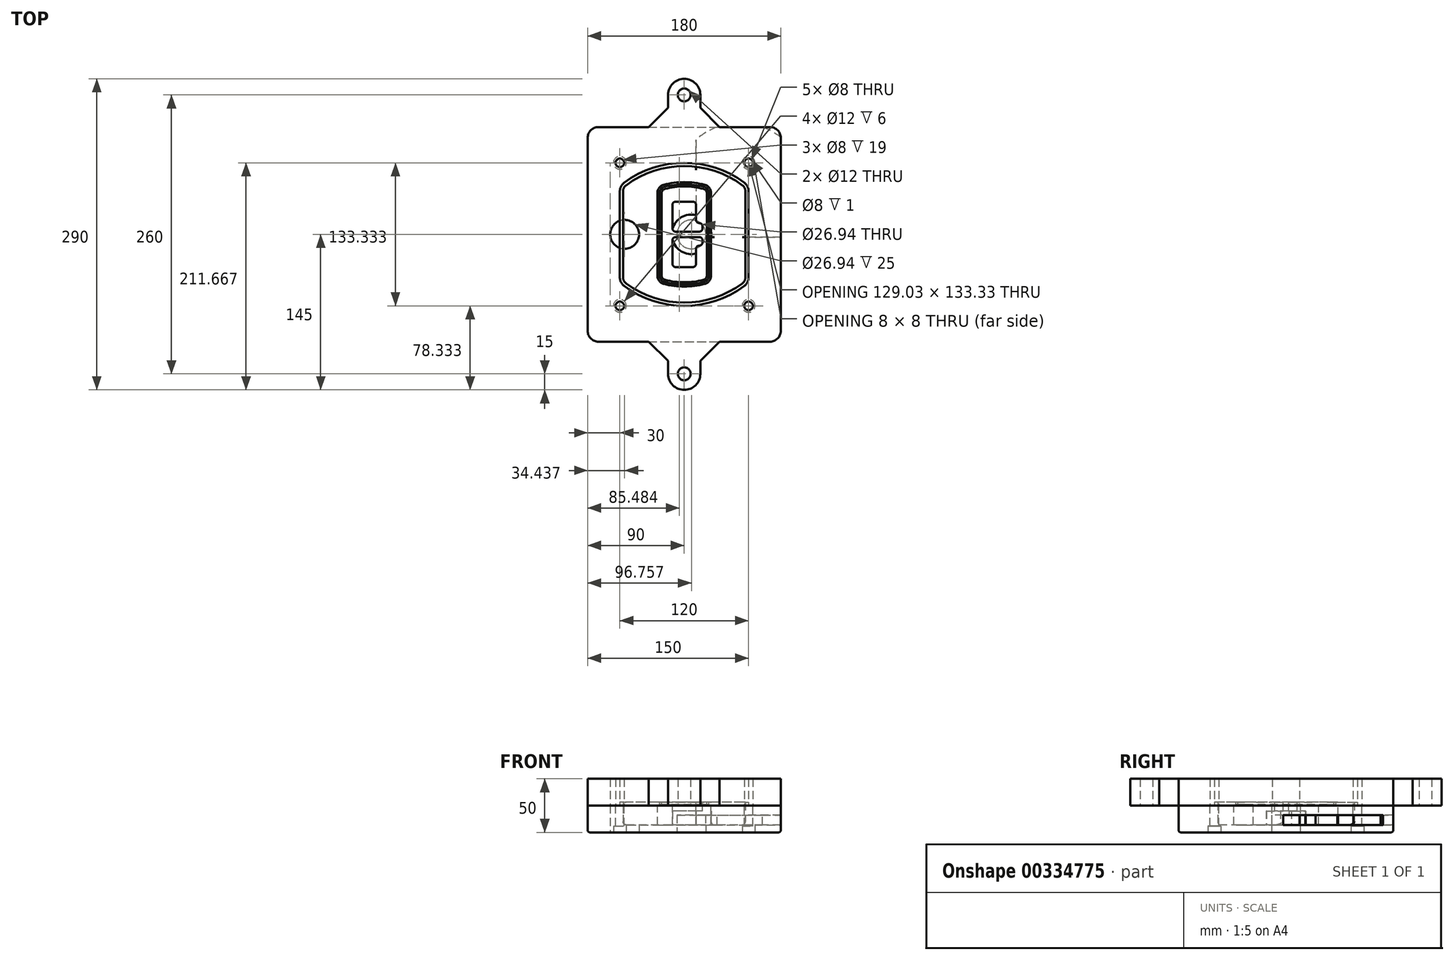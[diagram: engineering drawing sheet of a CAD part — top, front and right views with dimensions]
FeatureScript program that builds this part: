
annotation { "Feature Type Name" : "Feature", "Feature Type Description" : "" }
export const myFeature = defineFeature(function(context is Context, id is Id, definition is map)
    precondition{}
    {
        {
            var Q0;
            Q0=qCreatedBy(makeId("Top.planeOp"),FACE);
            var sketch = newSketch(context, id + "F0", { "sketchPlane" : qUnion([Q0])});
            skPoint(sketch, "E0.rect.middle", {"position": v(0, 0) * mm});
            skLineSegment(sketch, "E1.bottom", {"start": v(-80, -100) * mm, "end": v(80, -100) * mm});
            skLineSegment(sketch, "E1.top", {"start": v(-80, 100) * mm, "end": v(80, 100) * mm});
            skLineSegment(sketch, "E1.left", {"start": v(-90, -90) * mm, "end": v(-90, 90) * mm});
            skLineSegment(sketch, "E1.right", {"start": v(90, -90) * mm, "end": v(90, 90) * mm});
            skLineSegment(sketch, "E2", {"start": v(-90, 100) * mm, "end": v(90, -100) * mm, "construction": true});
            skLineSegment(sketch, "E3", {"start": v(90, 100) * mm, "end": v(-90, -100) * mm, "construction": true});
            skCircle(sketch, "E4", {"center": v(-60, 66.67) * mm, "radius": 4 * mm});
            skCircle(sketch, "E5", {"center": v(60, 66.67) * mm, "radius": 4 * mm});
            skCircle(sketch, "E6", {"center": v(60, -66.67) * mm, "radius": 4 * mm});
            skCircle(sketch, "E7", {"center": v(-60, -66.67) * mm, "radius": 4 * mm});
            skLineSegment(sketch, "E8", {"start": v(-60, 66.67) * mm, "end": v(60, 66.67) * mm, "construction": true});
            skLineSegment(sketch, "E9", {"start": v(60, 66.67) * mm, "end": v(60, -66.67) * mm, "construction": true});
            skLineSegment(sketch, "E10", {"start": v(60, -66.67) * mm, "end": v(-60, -66.67) * mm, "construction": true});
            skLineSegment(sketch, "E11", {"start": v(-60, -66.67) * mm, "end": v(-60, 66.67) * mm, "construction": true});
            skLineSegment(sketch, "E12", {"start": v(-60, 40.14) * mm, "end": v(-60, -40.14) * mm});
            skLineSegment(sketch, "E13", {"start": v(60, 40.14) * mm, "end": v(60, -40.14) * mm});
            skArc(sketch, "E14", {"start": v(55.96, 48.17) * mm, "mid": v(0, 66.67) * mm, "end": v(-55.96, 48.17) * mm});
            skArc(sketch, "E15", {"start": v(-55.96, -48.17) * mm, "mid": v(0, -66.67) * mm, "end": v(55.96, -48.17) * mm});
            skLineSegment(sketch, "E16", {"start": v(-60, 0) * mm, "end": v(60, 0) * mm, "construction": true});
            skPoint(sketch, "E17.visualSharp", {"position": v(-60, -45) * mm});
            skArc(sketch, "E17.filletArc", {"start": v(-60, -40.14) * mm, "mid": v(-58.93, -44.64) * mm, "end": v(-55.96, -48.17) * mm});
            skPoint(sketch, "E18.visualSharp", {"position": v(-60, 45) * mm});
            skArc(sketch, "E18.filletArc", {"start": v(-55.96, 48.17) * mm, "mid": v(-58.93, 44.64) * mm, "end": v(-60, 40.14) * mm});
            skPoint(sketch, "E19.visualSharp", {"position": v(60, 45) * mm});
            skArc(sketch, "E19.filletArc", {"start": v(60, 40.14) * mm, "mid": v(58.93, 44.64) * mm, "end": v(55.96, 48.17) * mm});
            skPoint(sketch, "E20.visualSharp", {"position": v(60, -45) * mm});
            skArc(sketch, "E20.filletArc", {"start": v(55.96, -48.17) * mm, "mid": v(58.93, -44.64) * mm, "end": v(60, -40.14) * mm});
            skPoint(sketch, "E21.visualSharp", {"position": v(-90, 100) * mm});
            skArc(sketch, "E21.filletArc", {"start": v(-80, 100) * mm, "mid": v(-87.07, 97.07) * mm, "end": v(-90, 90) * mm});
            skPoint(sketch, "E22.visualSharp", {"position": v(90, 100) * mm});
            skArc(sketch, "E22.filletArc", {"start": v(90, 90) * mm, "mid": v(87.07, 97.07) * mm, "end": v(80, 100) * mm});
            skPoint(sketch, "E23.visualSharp", {"position": v(90, -100) * mm});
            skArc(sketch, "E23.filletArc", {"start": v(80, -100) * mm, "mid": v(87.07, -97.07) * mm, "end": v(90, -90) * mm});
            skPoint(sketch, "E24.visualSharp", {"position": v(-90, -100) * mm});
            skArc(sketch, "E24.filletArc", {"start": v(-90, -90) * mm, "mid": v(-87.07, -97.07) * mm, "end": v(-80, -100) * mm});
            skArc(sketch, "E25.0", {"start": v(57, 40.14) * mm, "mid": v(56.25, 43.29) * mm, "end": v(54.17, 45.76) * mm});
            skLineSegment(sketch, "E25.1", {"start": v(57, 40.14) * mm, "end": v(57, -40.14) * mm});
            skArc(sketch, "E25.2", {"start": v(54.17, -45.76) * mm, "mid": v(56.25, -43.29) * mm, "end": v(57, -40.14) * mm});
            skArc(sketch, "E25.3", {"start": v(-54.17, -45.76) * mm, "mid": v(0, -63.67) * mm, "end": v(54.17, -45.76) * mm});
            skArc(sketch, "E25.4", {"start": v(-57, -40.14) * mm, "mid": v(-56.25, -43.29) * mm, "end": v(-54.17, -45.76) * mm});
            skArc(sketch, "E25.5", {"start": v(54.17, 45.76) * mm, "mid": v(0, 63.67) * mm, "end": v(-54.17, 45.76) * mm});
            skLineSegment(sketch, "E25.6", {"start": v(-57, 40.14) * mm, "end": v(-57, -40.14) * mm});
            skArc(sketch, "E25.7", {"start": v(-54.17, 45.76) * mm, "mid": v(-56.25, 43.29) * mm, "end": v(-57, 40.14) * mm});
            skArc(sketch, "E26.0", {"start": v(-58.34, 51.39) * mm, "mid": v(-62.5, 46.44) * mm, "end": v(-64, 40.14) * mm});
            skArc(sketch, "E26.1", {"start": v(58.34, 51.39) * mm, "mid": v(0, 70.67) * mm, "end": v(-58.34, 51.39) * mm});
            skArc(sketch, "E26.2", {"start": v(64, 40.14) * mm, "mid": v(62.5, 46.44) * mm, "end": v(58.34, 51.39) * mm});
            skLineSegment(sketch, "E26.3", {"start": v(64, 40.14) * mm, "end": v(64, -40.14) * mm});
            skArc(sketch, "E26.4", {"start": v(58.34, -51.39) * mm, "mid": v(62.5, -46.44) * mm, "end": v(64, -40.14) * mm});
            skLineSegment(sketch, "E26.5", {"start": v(-64, 40.14) * mm, "end": v(-64, -40.14) * mm});
            skArc(sketch, "E26.6", {"start": v(-58.34, -51.39) * mm, "mid": v(0, -70.67) * mm, "end": v(58.34, -51.39) * mm});
            skArc(sketch, "E26.7", {"start": v(-64, -40.14) * mm, "mid": v(-62.5, -46.44) * mm, "end": v(-58.34, -51.39) * mm});
            skSolve(sketch);
        }
        {
            var Q0;
            Q0=makeQuery(id+"F0.imprint","IMPRINT",FACE,{"disambiguationData":[TD([[makeQuery(id+"F0.imprint","IMPRINT",EDGE,{"derivedFrom":sQuery(id+"F0.wireOp",EDGE,"E1.bottom")}),1.0]])]});
            var Q1;
            Q1=makeQuery(id+"F0.imprint","IMPRINT",FACE,{"disambiguationData":[TD([[makeQuery(id+"F0.imprint","IMPRINT",EDGE,{"derivedFrom":sQuery(id+"F0.wireOp",EDGE,"E12")}),1.0]])]});
            var Q2;
            Q2=makeQuery(id+"F0.imprint","IMPRINT",FACE,{"disambiguationData":[TD([[makeQuery(id+"F0.imprint","IMPRINT",EDGE,{"derivedFrom":sQuery(id+"F0.wireOp",EDGE,"E25.0")}),1.0]])]});
            var Q3;
            Q3=makeQuery(id+"F0.imprint","IMPRINT",FACE,{"disambiguationData":[TD([[makeQuery(id+"F0.imprint","IMPRINT",EDGE,{"derivedFrom":sQuery(id+"F0.wireOp",EDGE,"E12")}),-1.0]])]});
            extrude(context, id + "F1", {"entities" : qUnion([Q0, Q1, Q2, Q3]), "oppositeDirection" : true, "depth" : 25 * mm});
        }
        {
            var Q0;
            Q0=makeQuery(id+"F0.imprint","IMPRINT",FACE,{"disambiguationData":[TD([[makeQuery(id+"F0.imprint","IMPRINT",EDGE,{"derivedFrom":sQuery(id+"F0.wireOp",EDGE,"E12")}),1.0]])]});
            extrude(context, id + "F2", {"entities" : qUnion([Q0]), "operationType" : NewBodyOperationType.ADD, "depth" : 3 * mm});
        }
        {
            var Q0;
            Q0=makeQuery(id+"F0.imprint","IMPRINT",FACE,{"disambiguationData":[TD([[makeQuery(id+"F0.imprint","IMPRINT",EDGE,{"derivedFrom":sQuery(id+"F0.wireOp",EDGE,"E25.0")}),1.0]])]});
            extrude(context, id + "F3", {"entities" : qUnion([Q0]), "operationType" : NewBodyOperationType.REMOVE, "oppositeDirection" : true, "depth" : 18 * mm});
        }
        {
            var Q0;
            Q0=makeQuery(id+"F2.opExtrude","CAP_FACE",FACE,{"disambiguationData":[OSD([sQuery(id+"F0.wireOp",EDGE,"E12"),sQuery(id+"F0.wireOp",EDGE,"E13"),sQuery(id+"F0.wireOp",EDGE,"E14"),sQuery(id+"F0.wireOp",EDGE,"E15"),sQuery(id+"F0.wireOp",EDGE,"E17.filletArc"),sQuery(id+"F0.wireOp",EDGE,"E18.filletArc"),sQuery(id+"F0.wireOp",EDGE,"E19.filletArc"),sQuery(id+"F0.wireOp",EDGE,"E20.filletArc"),sQuery(id+"F0.wireOp",EDGE,"E25.0"),sQuery(id+"F0.wireOp",EDGE,"E25.1"),sQuery(id+"F0.wireOp",EDGE,"E25.2"),sQuery(id+"F0.wireOp",EDGE,"E25.3"),sQuery(id+"F0.wireOp",EDGE,"E25.4"),sQuery(id+"F0.wireOp",EDGE,"E25.5"),sQuery(id+"F0.wireOp",EDGE,"E25.6"),sQuery(id+"F0.wireOp",EDGE,"E25.7")])],"isStart":false});
            var sketch = newSketch(context, id + "F4", { "sketchPlane" : qUnion([Q0])});
            skArc(sketch, "E27.0", {"start": v(-19, -46.25) * mm, "mid": v(0, -48.67) * mm, "end": v(19, -46.25) * mm});
            skArc(sketch, "E28.0", {"start": v(19, 46.25) * mm, "mid": v(0, 48.67) * mm, "end": v(-19, 46.25) * mm});
            skLineSegment(sketch, "E29", {"start": v(-25, 38.5) * mm, "end": v(-25, -38.5) * mm});
            skLineSegment(sketch, "E30", {"start": v(25, 38.5) * mm, "end": v(25, -38.5) * mm});
            skLineSegment(sketch, "E31", {"start": v(-25, 44.43) * mm, "end": v(25, 44.43) * mm, "construction": true});
            skLineSegment(sketch, "E32", {"start": v(-25, -44.43) * mm, "end": v(25, -44.43) * mm, "construction": true});
            skPoint(sketch, "E33.visualSharp", {"position": v(-25, 44.43) * mm});
            skArc(sketch, "E33.filletArc", {"start": v(-19, 46.25) * mm, "mid": v(-23.33, 43.4) * mm, "end": v(-25, 38.5) * mm});
            skPoint(sketch, "E34.visualSharp", {"position": v(25, 44.43) * mm});
            skArc(sketch, "E34.filletArc", {"start": v(25, 38.5) * mm, "mid": v(23.33, 43.4) * mm, "end": v(19, 46.25) * mm});
            skPoint(sketch, "E35.visualSharp", {"position": v(25, -44.43) * mm});
            skArc(sketch, "E35.filletArc", {"start": v(19, -46.25) * mm, "mid": v(23.33, -43.4) * mm, "end": v(25, -38.5) * mm});
            skPoint(sketch, "E36.visualSharp", {"position": v(-25, -44.43) * mm});
            skArc(sketch, "E36.filletArc", {"start": v(-25, -38.5) * mm, "mid": v(-23.33, -43.4) * mm, "end": v(-19, -46.25) * mm});
            skArc(sketch, "E37.0", {"start": v(54.17, 45.76) * mm, "mid": v(0, 63.67) * mm, "end": v(-54.17, 45.76) * mm});
            skArc(sketch, "E37.1", {"start": v(-54.17, 45.76) * mm, "mid": v(-56.25, 43.29) * mm, "end": v(-57, 40.14) * mm});
            skLineSegment(sketch, "E37.2", {"start": v(-57, 40.14) * mm, "end": v(-57, -40.14) * mm});
            skArc(sketch, "E37.3", {"start": v(-57, -40.14) * mm, "mid": v(-56.25, -43.29) * mm, "end": v(-54.17, -45.76) * mm});
            skArc(sketch, "E37.4", {"start": v(-54.17, -45.76) * mm, "mid": v(0, -63.67) * mm, "end": v(54.17, -45.76) * mm});
            skArc(sketch, "E37.5", {"start": v(54.17, -45.76) * mm, "mid": v(56.25, -43.29) * mm, "end": v(57, -40.14) * mm});
            skLineSegment(sketch, "E37.6", {"start": v(57, 40.14) * mm, "end": v(57, -40.14) * mm});
            skArc(sketch, "E37.7", {"start": v(57, 40.14) * mm, "mid": v(56.25, 43.29) * mm, "end": v(54.17, 45.76) * mm});
            skLineSegment(sketch, "E38.0", {"start": v(23, 38.5) * mm, "end": v(23, -38.5) * mm});
            skArc(sketch, "E38.1", {"start": v(18.5, -44.31) * mm, "mid": v(21.74, -42.18) * mm, "end": v(23, -38.5) * mm});
            skArc(sketch, "E38.2", {"start": v(-18.5, -44.31) * mm, "mid": v(0, -46.67) * mm, "end": v(18.5, -44.31) * mm});
            skArc(sketch, "E38.3", {"start": v(-23, -38.5) * mm, "mid": v(-21.74, -42.18) * mm, "end": v(-18.5, -44.31) * mm});
            skLineSegment(sketch, "E38.4", {"start": v(-23, 38.5) * mm, "end": v(-23, -38.5) * mm});
            skArc(sketch, "E38.5", {"start": v(23, 38.5) * mm, "mid": v(21.74, 42.18) * mm, "end": v(18.5, 44.31) * mm});
            skArc(sketch, "E38.6", {"start": v(-18.5, 44.31) * mm, "mid": v(-21.74, 42.18) * mm, "end": v(-23, 38.5) * mm});
            skArc(sketch, "E38.7", {"start": v(18.5, 44.31) * mm, "mid": v(0, 46.67) * mm, "end": v(-18.5, 44.31) * mm});
            skArc(sketch, "E39.0", {"start": v(21, 38.5) * mm, "mid": v(20.16, 40.95) * mm, "end": v(18, 42.38) * mm});
            skLineSegment(sketch, "E39.1", {"start": v(21, 38.5) * mm, "end": v(21, -38.5) * mm});
            skArc(sketch, "E39.2", {"start": v(18, -42.38) * mm, "mid": v(20.16, -40.95) * mm, "end": v(21, -38.5) * mm});
            skArc(sketch, "E39.3", {"start": v(-18, -42.38) * mm, "mid": v(0, -44.67) * mm, "end": v(18, -42.38) * mm});
            skArc(sketch, "E39.4", {"start": v(-21, -38.5) * mm, "mid": v(-20.16, -40.95) * mm, "end": v(-18, -42.38) * mm});
            skArc(sketch, "E39.5", {"start": v(18, 42.38) * mm, "mid": v(0, 44.67) * mm, "end": v(-18, 42.38) * mm});
            skLineSegment(sketch, "E39.6", {"start": v(-21, 38.5) * mm, "end": v(-21, -38.5) * mm});
            skArc(sketch, "E39.7", {"start": v(-18, 42.38) * mm, "mid": v(-20.16, 40.95) * mm, "end": v(-21, 38.5) * mm});
            skLineSegment(sketch, "E40", {"start": v(-25, 0) * mm, "end": v(25, 0) * mm, "construction": true});
            skLineSegment(sketch, "E41", {"start": v(-11, 5.5) * mm, "end": v(-11, 27.5) * mm});
            skLineSegment(sketch, "E42", {"start": v(-8, 30.5) * mm, "end": v(8, 30.5) * mm});
            skLineSegment(sketch, "E43", {"start": v(11, 27.5) * mm, "end": v(11, 13.5) * mm});
            skLineSegment(sketch, "E44", {"start": v(14, 10.5) * mm, "end": v(14, 10.5) * mm});
            skLineSegment(sketch, "E45", {"start": v(17, 7.5) * mm, "end": v(17, 5.5) * mm});
            skLineSegment(sketch, "E46", {"start": v(14, 2.5) * mm, "end": v(-8, 2.5) * mm});
            skPoint(sketch, "E47.visualSharp", {"position": v(-11, 30.5) * mm});
            skArc(sketch, "E47.filletArc", {"start": v(-8, 30.5) * mm, "mid": v(-10.12, 29.62) * mm, "end": v(-11, 27.5) * mm});
            skPoint(sketch, "E48.visualSharp", {"position": v(11, 30.5) * mm});
            skArc(sketch, "E48.filletArc", {"start": v(11, 27.5) * mm, "mid": v(10.12, 29.62) * mm, "end": v(8, 30.5) * mm});
            skPoint(sketch, "E49.visualSharp", {"position": v(11, 10.5) * mm});
            skArc(sketch, "E49.filletArc", {"start": v(11, 13.5) * mm, "mid": v(11.88, 11.38) * mm, "end": v(14, 10.5) * mm});
            skPoint(sketch, "E50.visualSharp", {"position": v(17, 10.5) * mm});
            skArc(sketch, "E50.filletArc", {"start": v(17, 7.5) * mm, "mid": v(16.12, 9.62) * mm, "end": v(14, 10.5) * mm});
            skPoint(sketch, "E51.visualSharp", {"position": v(17, 2.5) * mm});
            skArc(sketch, "E51.filletArc", {"start": v(14, 2.5) * mm, "mid": v(16.12, 3.38) * mm, "end": v(17, 5.5) * mm});
            skPoint(sketch, "E52.visualSharp", {"position": v(-11, 2.5) * mm});
            skArc(sketch, "E52.filletArc", {"start": v(-11, 5.5) * mm, "mid": v(-10.12, 3.38) * mm, "end": v(-8, 2.5) * mm});
            skLineSegment(sketch, "E53.0.MirrorCS", {"start": v(14, -2.5) * mm, "end": v(-8, -2.5) * mm});
            skArc(sketch, "E54.0.MirrorCS", {"start": v(-11, -5.5) * mm, "mid": v(-10.12, -3.38) * mm, "end": v(-8, -2.5) * mm});
            skLineSegment(sketch, "E55.0.MirrorCS", {"start": v(-11, -5.5) * mm, "end": v(-11, -27.5) * mm});
            skArc(sketch, "E56.0.MirrorCS", {"start": v(-8, -30.5) * mm, "mid": v(-10.12, -29.62) * mm, "end": v(-11, -27.5) * mm});
            skLineSegment(sketch, "E57.0.MirrorCS", {"start": v(-8, -30.5) * mm, "end": v(8, -30.5) * mm});
            skArc(sketch, "E58.0.MirrorCS", {"start": v(11, -27.5) * mm, "mid": v(10.12, -29.62) * mm, "end": v(8, -30.5) * mm});
            skLineSegment(sketch, "E59.0.MirrorCS", {"start": v(11, -27.5) * mm, "end": v(11, -13.5) * mm});
            skArc(sketch, "E60.0.MirrorCS", {"start": v(11, -13.5) * mm, "mid": v(11.88, -11.38) * mm, "end": v(14, -10.5) * mm});
            skArc(sketch, "E61.0.MirrorCS", {"start": v(17, -7.5) * mm, "mid": v(16.12, -9.62) * mm, "end": v(14, -10.5) * mm});
            skLineSegment(sketch, "E62.0.MirrorCS", {"start": v(17, -7.5) * mm, "end": v(17, -5.5) * mm});
            skArc(sketch, "E63.0.MirrorCS", {"start": v(14, -2.5) * mm, "mid": v(16.12, -3.38) * mm, "end": v(17, -5.5) * mm});
            skSolve(sketch);
        }
        {
            var Q0;
            Q0=makeQuery(id+"F4.imprint","IMPRINT",FACE,{"disambiguationData":[TD([[makeQuery(id+"F4.imprint","IMPRINT",EDGE,{"derivedFrom":sQuery(id+"F4.wireOp",EDGE,"E27.0")}),1.0]])]});
            var Q1;
            Q1=makeQuery(id+"F4.imprint","IMPRINT",FACE,{"disambiguationData":[TD([[makeQuery(id+"F4.imprint","IMPRINT",EDGE,{"derivedFrom":sQuery(id+"F4.wireOp",EDGE,"E38.0")}),-1.0]])]});
            var Q2;
            Q2=makeQuery(id+"F4.imprint","IMPRINT",FACE,{"disambiguationData":[TD([[makeQuery(id+"F4.imprint","IMPRINT",EDGE,{"derivedFrom":sQuery(id+"F4.wireOp",EDGE,"E39.0")}),1.0]])]});
            extrude(context, id + "F5", {"entities" : qUnion([Q0, Q1, Q2]), "operationType" : NewBodyOperationType.ADD, "endBound" : BoundingType.UP_TO_NEXT, "oppositeDirection" : true, "depth" : 25 * mm});
        }
        {
            var Q0;
            Q0=makeQuery(id+"F4.imprint","IMPRINT",FACE,{"disambiguationData":[TD([[makeQuery(id+"F4.imprint","IMPRINT",EDGE,{"derivedFrom":sQuery(id+"F4.wireOp",EDGE,"E38.0")}),-1.0]])]});
            extrude(context, id + "F6", {"entities" : qUnion([Q0]), "operationType" : NewBodyOperationType.REMOVE, "oppositeDirection" : true, "depth" : 2 * mm});
        }
        {
            var Q0;
            Q0=makeQuery(id+"F1.opExtrude","CAP_FACE",FACE,{"disambiguationData":[OSD([sQuery(id+"F0.wireOp",EDGE,"E1.bottom"),sQuery(id+"F0.wireOp",EDGE,"E1.top"),sQuery(id+"F0.wireOp",EDGE,"E1.left"),sQuery(id+"F0.wireOp",EDGE,"E1.right"),sQuery(id+"F0.wireOp",EDGE,"E4"),sQuery(id+"F0.wireOp",EDGE,"E5"),sQuery(id+"F0.wireOp",EDGE,"E6"),sQuery(id+"F0.wireOp",EDGE,"E7"),sQuery(id+"F0.wireOp",EDGE,"E21.filletArc"),sQuery(id+"F0.wireOp",EDGE,"E22.filletArc"),sQuery(id+"F0.wireOp",EDGE,"E23.filletArc"),sQuery(id+"F0.wireOp",EDGE,"E24.filletArc")])],"isStart":false});
            var sketch = newSketch(context, id + "F7", { "sketchPlane" : qUnion([Q0])});
            skCircle(sketch, "E64", {"center": v(6.76, 0) * mm, "radius": 13.47 * mm});
            skCircle(sketch, "E65", {"center": v(-55.56, 0) * mm, "radius": 13.47 * mm});
            skLineSegment(sketch, "E66", {"start": v(90, 0) * mm, "end": v(-90, 0) * mm});
            skCircle(sketch, "E67", {"center": v(6.76, 0) * mm, "radius": 18.47 * mm});
            skCircle(sketch, "E68", {"center": v(60, -66.67) * mm, "radius": 6 * mm});
            skCircle(sketch, "E69", {"center": v(-60, -66.67) * mm, "radius": 6 * mm});
            skCircle(sketch, "E70", {"center": v(-60, 66.67) * mm, "radius": 6 * mm});
            skCircle(sketch, "E71", {"center": v(60, 66.67) * mm, "radius": 6 * mm});
            skSolve(sketch);
        }
        {
            var Q0;
            {var subQ1=sQuery(id+"F7.wireOp",EDGE,"E66");var subQ4=sQuery(id+"F7.wireOp",EDGE,"E64");var subQ6=makeQuery(id+"F7.imprint","INTERSECT",VERTEX,{"disambiguationData":[OD(0.0)],"derivedFrom":[subQ4,subQ1]});Q0=makeQuery(id+"F7.imprint","IMPRINT",FACE,{"disambiguationData":[TD([[makeQuery(id+"F7.imprint","IMPRINT",EDGE,{"disambiguationData":[TD([[subQ6,-1.0]])],"derivedFrom":subQ4}),-1.0]])]});}
            var Q1;
            {var subQ0=sQuery(id+"F7.wireOp",EDGE,"E66");var subQ1=sQuery(id+"F7.wireOp",EDGE,"E64");var subQ3=makeQuery(id+"F7.imprint","INTERSECT",VERTEX,{"disambiguationData":[OD(0.0)],"derivedFrom":[subQ1,subQ0]});Q1=makeQuery(id+"F7.imprint","IMPRINT",FACE,{"disambiguationData":[TD([[makeQuery(id+"F7.imprint","IMPRINT",EDGE,{"disambiguationData":[TD([[subQ3,-1.0]])],"derivedFrom":subQ1}),1.0]])]});}
            var Q2;
            {var subQ0=sQuery(id+"F7.wireOp",EDGE,"E66");var subQ1=sQuery(id+"F7.wireOp",EDGE,"E64");var subQ3=makeQuery(id+"F7.imprint","INTERSECT",VERTEX,{"disambiguationData":[OD(0.0)],"derivedFrom":[subQ1,subQ0]});Q2=makeQuery(id+"F7.imprint","IMPRINT",FACE,{"disambiguationData":[TD([[makeQuery(id+"F7.imprint","IMPRINT",EDGE,{"disambiguationData":[TD([[subQ3,1.0]])],"derivedFrom":subQ1}),1.0]])]});}
            var Q3;
            {var subQ1=sQuery(id+"F7.wireOp",EDGE,"E66");var subQ4=sQuery(id+"F7.wireOp",EDGE,"E64");var subQ6=makeQuery(id+"F7.imprint","INTERSECT",VERTEX,{"disambiguationData":[OD(0.0)],"derivedFrom":[subQ4,subQ1]});Q3=makeQuery(id+"F7.imprint","IMPRINT",FACE,{"disambiguationData":[TD([[makeQuery(id+"F7.imprint","IMPRINT",EDGE,{"disambiguationData":[TD([[subQ6,1.0]])],"derivedFrom":subQ4}),-1.0]])]});}
            extrude(context, id + "F8", {"entities" : qUnion([Q0, Q1, Q2, Q3]), "operationType" : NewBodyOperationType.ADD, "oppositeDirection" : true, "depth" : 20 * mm});
        }
        {
            var Q0;
            {var subQ0=sQuery(id+"F7.wireOp",EDGE,"E66");var subQ1=sQuery(id+"F7.wireOp",EDGE,"E64");var subQ3=makeQuery(id+"F7.imprint","INTERSECT",VERTEX,{"disambiguationData":[OD(0.0)],"derivedFrom":[subQ1,subQ0]});Q0=makeQuery(id+"F7.imprint","IMPRINT",FACE,{"disambiguationData":[TD([[makeQuery(id+"F7.imprint","IMPRINT",EDGE,{"disambiguationData":[TD([[subQ3,-1.0]])],"derivedFrom":subQ1}),1.0]])]});}
            var Q1;
            {var subQ0=sQuery(id+"F7.wireOp",EDGE,"E66");var subQ1=sQuery(id+"F7.wireOp",EDGE,"E64");var subQ3=makeQuery(id+"F7.imprint","INTERSECT",VERTEX,{"disambiguationData":[OD(0.0)],"derivedFrom":[subQ1,subQ0]});Q1=makeQuery(id+"F7.imprint","IMPRINT",FACE,{"disambiguationData":[TD([[makeQuery(id+"F7.imprint","IMPRINT",EDGE,{"disambiguationData":[TD([[subQ3,1.0]])],"derivedFrom":subQ1}),1.0]])]});}
            extrude(context, id + "F9", {"entities" : qUnion([Q0, Q1]), "operationType" : NewBodyOperationType.REMOVE, "oppositeDirection" : true, "depth" : 16 * mm});
        }
        {
            var Q0;
            {var subQ0=sQuery(id+"F7.wireOp",EDGE,"E66");var subQ1=sQuery(id+"F7.wireOp",EDGE,"E65");var subQ3=makeQuery(id+"F7.imprint","INTERSECT",VERTEX,{"disambiguationData":[OD(0.0)],"derivedFrom":[subQ1,subQ0]});Q0=makeQuery(id+"F7.imprint","IMPRINT",FACE,{"disambiguationData":[TD([[makeQuery(id+"F7.imprint","IMPRINT",EDGE,{"disambiguationData":[TD([[subQ3,-1.0]])],"derivedFrom":subQ1}),1.0]])]});}
            var Q1;
            {var subQ0=sQuery(id+"F7.wireOp",EDGE,"E66");var subQ1=sQuery(id+"F7.wireOp",EDGE,"E65");var subQ3=makeQuery(id+"F7.imprint","INTERSECT",VERTEX,{"disambiguationData":[OD(0.0)],"derivedFrom":[subQ1,subQ0]});Q1=makeQuery(id+"F7.imprint","IMPRINT",FACE,{"disambiguationData":[TD([[makeQuery(id+"F7.imprint","IMPRINT",EDGE,{"disambiguationData":[TD([[subQ3,1.0]])],"derivedFrom":subQ1}),1.0]])]});}
            extrude(context, id + "F10", {"entities" : qUnion([Q0, Q1]), "operationType" : NewBodyOperationType.REMOVE, "oppositeDirection" : true, "depth" : 25 * mm});
        }
        {
            var Q0;
            Q0=makeQuery(id+"F7.imprint","IMPRINT",FACE,{"disambiguationData":[TD([[makeQuery(id+"F7.imprint","IMPRINT",EDGE,{"derivedFrom":sQuery(id+"F7.wireOp",EDGE,"E68")}),1.0]])]});
            var Q1;
            Q1=makeQuery(id+"F7.imprint","IMPRINT",FACE,{"disambiguationData":[TD([[makeQuery(id+"F7.imprint","IMPRINT",EDGE,{"derivedFrom":makeQuery(id+"F1.opExtrude","CAP_EDGE",EDGE,{"disambiguationData":[OSD([sQuery(id+"F0.wireOp",EDGE,"E5")])],"isStart":false})}),-1.0]])]});
            var Q2;
            Q2=makeQuery(id+"F7.imprint","IMPRINT",FACE,{"disambiguationData":[TD([[makeQuery(id+"F7.imprint","IMPRINT",EDGE,{"derivedFrom":sQuery(id+"F7.wireOp",EDGE,"E69")}),1.0]])]});
            var Q3;
            Q3=makeQuery(id+"F7.imprint","IMPRINT",FACE,{"disambiguationData":[TD([[makeQuery(id+"F7.imprint","IMPRINT",EDGE,{"derivedFrom":makeQuery(id+"F1.opExtrude","CAP_EDGE",EDGE,{"disambiguationData":[OSD([sQuery(id+"F0.wireOp",EDGE,"E4")])],"isStart":false})}),-1.0]])]});
            var Q4;
            Q4=makeQuery(id+"F7.imprint","IMPRINT",FACE,{"disambiguationData":[TD([[makeQuery(id+"F7.imprint","IMPRINT",EDGE,{"derivedFrom":sQuery(id+"F7.wireOp",EDGE,"E70")}),1.0]])]});
            var Q5;
            Q5=makeQuery(id+"F7.imprint","IMPRINT",FACE,{"disambiguationData":[TD([[makeQuery(id+"F7.imprint","IMPRINT",EDGE,{"derivedFrom":makeQuery(id+"F1.opExtrude","CAP_EDGE",EDGE,{"disambiguationData":[OSD([sQuery(id+"F0.wireOp",EDGE,"E7")])],"isStart":false})}),-1.0]])]});
            var Q6;
            Q6=makeQuery(id+"F7.imprint","IMPRINT",FACE,{"disambiguationData":[TD([[makeQuery(id+"F7.imprint","IMPRINT",EDGE,{"derivedFrom":sQuery(id+"F7.wireOp",EDGE,"E71")}),1.0]])]});
            var Q7;
            Q7=makeQuery(id+"F7.imprint","IMPRINT",FACE,{"disambiguationData":[TD([[makeQuery(id+"F7.imprint","IMPRINT",EDGE,{"derivedFrom":makeQuery(id+"F1.opExtrude","CAP_EDGE",EDGE,{"disambiguationData":[OSD([sQuery(id+"F0.wireOp",EDGE,"E6")])],"isStart":false})}),-1.0]])]});
            extrude(context, id + "F11", {"entities" : qUnion([Q0, Q1, Q2, Q3, Q4, Q5, Q6, Q7]), "operationType" : NewBodyOperationType.REMOVE, "oppositeDirection" : true, "depth" : 6 * mm});
        }
        {
            var Q0;
            Q0=makeQuery(id+"F9.boolean.opBoolean","COPY",FACE,{"derivedFrom":makeQuery(id+"F9.opExtrude","CAP_FACE",FACE,{"disambiguationData":[OSD([sQuery(id+"F7.wireOp",EDGE,"E64")])],"isStart":false})});
            var sketch = newSketch(context, id + "F12", { "sketchPlane" : qUnion([Q0])});
            skArc(sketch, "E72.0", {"start": v(11, -88.19) * mm, "mid": v(97.1, -83.6) * mm, "end": v(92.5, 2.5) * mm});
            skLineSegment(sketch, "E72.1", {"start": v(11, -17.97) * mm, "end": v(11, -17.97) * mm});
            skLineSegment(sketch, "E73", {"start": v(92.5, -105.13) * mm, "end": v(102.3, -105.13) * mm});
            skLineSegment(sketch, "E74.0", {"start": v(92.5, 2.5) * mm, "end": v(14, 2.5) * mm});
            skArc(sketch, "E74.1", {"start": v(14, 2.5) * mm, "mid": v(16.12, 3.38) * mm, "end": v(17, 5.5) * mm});
            skLineSegment(sketch, "E74.2", {"start": v(17, 7.5) * mm, "end": v(17, 5.5) * mm});
            skArc(sketch, "E74.3", {"start": v(17, 7.5) * mm, "mid": v(16.12, 9.62) * mm, "end": v(14, 10.5) * mm});
            skArc(sketch, "E74.4", {"start": v(11, 13.5) * mm, "mid": v(11.88, 11.38) * mm, "end": v(14, 10.5) * mm});
            skLineSegment(sketch, "E74.5", {"start": v(11, 13.5) * mm, "end": v(11, -88.19) * mm});
            skLineSegment(sketch, "E74.7", {"start": v(92.5, -2.5) * mm, "end": v(14, -2.5) * mm});
            skArc(sketch, "E74.8", {"start": v(14, -2.5) * mm, "mid": v(16.12, -3.38) * mm, "end": v(17, -5.5) * mm});
            skLineSegment(sketch, "E74.9", {"start": v(17, -7.5) * mm, "end": v(17, -5.5) * mm});
            skArc(sketch, "E74.10", {"start": v(17, -7.5) * mm, "mid": v(16.12, -9.62) * mm, "end": v(14, -10.5) * mm});
            skArc(sketch, "E74.11", {"start": v(11, -13.5) * mm, "mid": v(11.88, -11.38) * mm, "end": v(14, -10.5) * mm});
            skLineSegment(sketch, "E74.12", {"start": v(11, -17.97) * mm, "end": v(11, -13.5) * mm});
            skPoint(sketch, "E75.orphan", {"position": v(11, -27.5) * mm});
            skPoint(sketch, "E76.orphan", {"position": v(-8, -2.5) * mm});
            skPoint(sketch, "E77.orphan", {"position": v(-8, 2.5) * mm});
            skPoint(sketch, "E78.orphan", {"position": v(11, 27.5) * mm});
            skSolve(sketch);
        }
        {
            var Q0;
            {var subQ7=sQuery(id+"F12.wireOp",EDGE,"E72.0");var subQ14=sQuery(id+"F12.wireOp",EDGE,"E72.1");var subQ16=sQuery(id+"F12.wireOp",EDGE,"E74.1");var subQ18=sQuery(id+"F12.wireOp",EDGE,"E74.8");Q0=qUnion([makeQuery(id+"F12.imprint","IMPRINT",FACE,{"disambiguationData":[TD([[makeQuery(id+"F12.imprint","IMPRINT",EDGE,{"derivedFrom":subQ7}),1.0]])]}),makeQuery(id+"F12.imprint","IMPRINT",FACE,{"disambiguationData":[TD([[makeQuery(id+"F12.imprint","IMPRINT",EDGE,{"derivedFrom":subQ14}),1.0]])]}),makeQuery(id+"F12.imprint","IMPRINT",FACE,{"disambiguationData":[TD([[makeQuery(id+"F12.imprint","IMPRINT",EDGE,{"derivedFrom":subQ16}),1.0]])]}),makeQuery(id+"F12.imprint","IMPRINT",FACE,{"disambiguationData":[TD([[makeQuery(id+"F12.imprint","IMPRINT",EDGE,{"derivedFrom":subQ18}),-1.0]])]})]);}
            var Q1;
            Q1=makeQuery(id+"F5.boolean.opBoolean","SPLIT",FACE,{"disambiguationData":[TD([makeQuery(id+"F5.opExtrude","SWEPT_FACE",FACE,{"disambiguationData":[OSD([sQuery(id+"F4.wireOp",EDGE,"E41")])]})])],"derivedFrom":makeQuery(id+"F3.boolean.opBoolean","COPY",FACE,{"derivedFrom":makeQuery(id+"F3.opExtrude","CAP_FACE",FACE,{"disambiguationData":[OSD([sQuery(id+"F0.wireOp",EDGE,"E25.0"),sQuery(id+"F0.wireOp",EDGE,"E25.1"),sQuery(id+"F0.wireOp",EDGE,"E25.2"),sQuery(id+"F0.wireOp",EDGE,"E25.3"),sQuery(id+"F0.wireOp",EDGE,"E25.4"),sQuery(id+"F0.wireOp",EDGE,"E25.5"),sQuery(id+"F0.wireOp",EDGE,"E25.6"),sQuery(id+"F0.wireOp",EDGE,"E25.7")])],"isStart":false})})});
            extrude(context, id + "F13", {"entities" : qUnion([Q0]), "operationType" : NewBodyOperationType.REMOVE, "endBound" : BoundingType.UP_TO_SURFACE, "endBoundEntityFace" : qUnion([Q1]), "depth" : 25 * mm});
        }
        {
            var Q0;
            Q0=makeQuery(id+"F3.boolean.opBoolean","COPY",EDGE,{"derivedFrom":makeQuery(id+"F3.opExtrude","CAP_EDGE",EDGE,{"disambiguationData":[OSD([sQuery(id+"F0.wireOp",EDGE,"E25.6")])],"isStart":false})});
            var Q1;
            Q1=makeQuery(id+"F8.boolean.opBoolean","INTERSECT",EDGE,{"derivedFrom":[makeQuery(id+"F5.opExtrude","SWEPT_FACE",FACE,{"disambiguationData":[OSD([sQuery(id+"F4.wireOp",EDGE,"E30")])]}),makeQuery(id+"F8.opExtrude","CAP_FACE",FACE,{"disambiguationData":[OSD([sQuery(id+"F7.wireOp",EDGE,"E67")])],"isStart":false})]});
            var Q2;
            Q2=makeQuery(id+"F8.boolean.opBoolean","INTERSECT",EDGE,{"disambiguationData":[OD(1.0)],"derivedFrom":[makeQuery(id+"F5.opExtrude","SWEPT_FACE",FACE,{"disambiguationData":[OSD([sQuery(id+"F4.wireOp",EDGE,"E30")])]}),makeQuery(id+"F8.opExtrude","SWEPT_FACE",FACE,{"disambiguationData":[OSD([sQuery(id+"F7.wireOp",EDGE,"E67")])]})]});
            var Q3;
            {var subQ0=makeQuery(id+"F3.boolean.opBoolean","COPY",FACE,{"derivedFrom":makeQuery(id+"F3.opExtrude","CAP_FACE",FACE,{"disambiguationData":[OSD([sQuery(id+"F0.wireOp",EDGE,"E25.0"),sQuery(id+"F0.wireOp",EDGE,"E25.1"),sQuery(id+"F0.wireOp",EDGE,"E25.2"),sQuery(id+"F0.wireOp",EDGE,"E25.3"),sQuery(id+"F0.wireOp",EDGE,"E25.4"),sQuery(id+"F0.wireOp",EDGE,"E25.5"),sQuery(id+"F0.wireOp",EDGE,"E25.6"),sQuery(id+"F0.wireOp",EDGE,"E25.7")])],"isStart":false})});var subQ1=sQuery(id+"F4.wireOp",EDGE,"E30");Q3=makeQuery(id+"F8.boolean.opBoolean","SPLIT",EDGE,{"disambiguationData":[TD([makeQuery(id+"F5.opExtrude","SWEPT_FACE",FACE,{"disambiguationData":[OSD([sQuery(id+"F4.wireOp",EDGE,"E35.filletArc")])]})])],"derivedFrom":makeQuery(id+"F5.opExtrude","TWEAK_EDGE",EDGE,{"derivedFrom":[subQ0,makeQuery(id+"F4.imprint","IMPRINT",EDGE,{"derivedFrom":subQ1})]})});}
            var Q4;
            {var subQ0=sQuery(id+"F0.wireOp",EDGE,"E25.0");var subQ1=sQuery(id+"F0.wireOp",EDGE,"E25.1");var subQ2=sQuery(id+"F0.wireOp",EDGE,"E25.2");var subQ3=sQuery(id+"F0.wireOp",EDGE,"E25.3");var subQ4=sQuery(id+"F0.wireOp",EDGE,"E25.4");var subQ5=sQuery(id+"F0.wireOp",EDGE,"E25.5");var subQ6=sQuery(id+"F0.wireOp",EDGE,"E25.6");var subQ7=sQuery(id+"F0.wireOp",EDGE,"E25.7");Q4=makeQuery(id+"F8.boolean.opBoolean","INTERSECT",EDGE,{"derivedFrom":[makeQuery(id+"F5.boolean.opBoolean","SPLIT",FACE,{"disambiguationData":[TD([makeQuery(id+"F2.opExtrude","SWEPT_FACE",FACE,{"disambiguationData":[OSD([subQ0])]})])],"derivedFrom":makeQuery(id+"F3.boolean.opBoolean","COPY",FACE,{"derivedFrom":makeQuery(id+"F3.opExtrude","CAP_FACE",FACE,{"disambiguationData":[OSD([subQ0,subQ1,subQ2,subQ3,subQ4,subQ5,subQ6,subQ7])],"isStart":false})})}),makeQuery(id+"F8.opExtrude","SWEPT_FACE",FACE,{"disambiguationData":[OSD([sQuery(id+"F7.wireOp",EDGE,"E67")])]})]});}
            var Q5;
            Q5=makeQuery(id+"F8.boolean.opBoolean","INTERSECT",EDGE,{"disambiguationData":[OD(0.0)],"derivedFrom":[makeQuery(id+"F5.opExtrude","SWEPT_FACE",FACE,{"disambiguationData":[OSD([sQuery(id+"F4.wireOp",EDGE,"E30")])]}),makeQuery(id+"F8.opExtrude","SWEPT_FACE",FACE,{"disambiguationData":[OSD([sQuery(id+"F7.wireOp",EDGE,"E67")])]})]});
            fillet(context, id + "F14", {"entities" : qUnion([Q0, Q1, Q2, Q3, Q4, Q5]), "radius" : 3 * mm, "tangentPropagation" : true, "allowEdgeOverflow" : false});
        }
        {
            var Q0;
            Q0=makeQuery(id+"F1.opExtrude","CAP_EDGE",EDGE,{"disambiguationData":[OSD([sQuery(id+"F0.wireOp",EDGE,"E1.bottom")])],"isStart":false});
            fillet(context, id + "F15", {"entities" : qUnion([Q0]), "radius" : 2 * mm, "tangentPropagation" : true, "allowEdgeOverflow" : false});
        }
        {
            var Q0;
            {var subQ0=sQuery(id+"F0.wireOp",EDGE,"E21.filletArc");var subQ1=sQuery(id+"F0.wireOp",EDGE,"E7");var subQ2=sQuery(id+"F0.wireOp",EDGE,"E6");var subQ3=sQuery(id+"F0.wireOp",EDGE,"E5");var subQ4=sQuery(id+"F0.wireOp",EDGE,"E4");var subQ5=sQuery(id+"F0.wireOp",EDGE,"E22.filletArc");var subQ6=sQuery(id+"F0.wireOp",EDGE,"E1.bottom");var subQ7=sQuery(id+"F0.wireOp",EDGE,"E1.right");var subQ8=sQuery(id+"F0.wireOp",EDGE,"E1.top");var subQ9=sQuery(id+"F0.wireOp",EDGE,"E1.left");var subQ10=sQuery(id+"F0.wireOp",EDGE,"E23.filletArc");var subQ11=sQuery(id+"F0.wireOp",EDGE,"E24.filletArc");Q0=makeQuery(id+"F2.boolean.opBoolean","SPLIT",FACE,{"disambiguationData":[TD([makeQuery(id+"F1.opExtrude","SWEPT_FACE",FACE,{"disambiguationData":[OSD([subQ6])]})])],"derivedFrom":makeQuery(id+"F1.opExtrude","CAP_FACE",FACE,{"disambiguationData":[OSD([subQ6,subQ8,subQ9,subQ7,subQ4,subQ3,subQ2,subQ1,subQ0,subQ5,subQ10,subQ11])],"isStart":true})});}
            var sketch = newSketch(context, id + "F16", { "sketchPlane" : qUnion([Q0])});
            skLineSegment(sketch, "E79", {"start": v(0, 100) * mm, "end": v(0, 130) * mm, "construction": true});
            skCircle(sketch, "E80", {"center": v(0, 130) * mm, "radius": 6 * mm});
            skLineSegment(sketch, "E81", {"start": v(-33, 100) * mm, "end": v(-15, 118) * mm});
            skLineSegment(sketch, "E82", {"start": v(-15, 118) * mm, "end": v(-15, 130) * mm});
            skLineSegment(sketch, "E83", {"start": v(15, 118) * mm, "end": v(15, 130) * mm});
            skArc(sketch, "E84", {"start": v(15, 130) * mm, "mid": v(0, 145) * mm, "end": v(-15, 130) * mm});
            skLineSegment(sketch, "E85", {"start": v(15, 118) * mm, "end": v(33, 100) * mm});
            skLineSegment(sketch, "E86", {"start": v(-90, 0) * mm, "end": v(90, 0) * mm, "construction": true});
            skLineSegment(sketch, "E87.MirrorCS", {"start": v(-15, 118) * mm, "end": v(-33, 100) * mm});
            skArc(sketch, "E88.MirrorCS", {"start": v(-15, 130) * mm, "mid": v(0, 145) * mm, "end": v(15, 130) * mm});
            skLineSegment(sketch, "E89.MirrorCS", {"start": v(33, 100) * mm, "end": v(15, 118) * mm});
            skLineSegment(sketch, "E90.MirrorCS", {"start": v(15, -118) * mm, "end": v(15, -130) * mm});
            skLineSegment(sketch, "E91.MirrorCS", {"start": v(-15, -118) * mm, "end": v(-15, -130) * mm});
            skLineSegment(sketch, "E92.MirrorCS", {"start": v(-33, -100) * mm, "end": v(-15, -118) * mm});
            skArc(sketch, "E93.MirrorCS", {"start": v(-15, -130) * mm, "mid": v(0, -145) * mm, "end": v(15, -130) * mm});
            skLineSegment(sketch, "E94.MirrorCS", {"start": v(33, -100) * mm, "end": v(15, -118) * mm});
            skCircle(sketch, "E95.MirrorC", {"center": v(0, -130) * mm, "radius": 6 * mm});
            skLineSegment(sketch, "E96.MirrorCS", {"start": v(-15, -118) * mm, "end": v(-33, -100) * mm});
            skLineSegment(sketch, "E97.MirrorCS", {"start": v(15, -118) * mm, "end": v(33, -100) * mm});
            skArc(sketch, "E98.MirrorCS", {"start": v(15, -130) * mm, "mid": v(0, -145) * mm, "end": v(-15, -130) * mm});
            skLineSegment(sketch, "E99.MirrorCS", {"start": v(0, -100) * mm, "end": v(0, -130) * mm, "construction": true});
            skSolve(sketch);
        }
        {
            var Q0;
            Q0=makeQuery(id+"F16.imprint","IMPRINT",FACE,{"disambiguationData":[TD([[makeQuery(id+"F16.imprint","IMPRINT",EDGE,{"derivedFrom":makeQuery(id+"F1.opExtrude","CAP_EDGE",EDGE,{"disambiguationData":[OSD([sQuery(id+"F0.wireOp",EDGE,"E1.left")])],"isStart":true})}),-1.0]])]});
            var Q1;
            Q1=makeQuery(id+"F16.imprint","IMPRINT",FACE,{"disambiguationData":[TD([[makeQuery(id+"F16.imprint","IMPRINT",EDGE,{"derivedFrom":sQuery(id+"F16.wireOp",EDGE,"E83")}),1.0]])]});
            var Q2;
            Q2=makeQuery(id+"F16.imprint","IMPRINT",FACE,{"disambiguationData":[TD([[makeQuery(id+"F16.imprint","IMPRINT",EDGE,{"derivedFrom":sQuery(id+"F16.wireOp",EDGE,"E90.MirrorCS")}),-1.0]])]});
            extrude(context, id + "F17", {"entities" : qUnion([Q0, Q1, Q2]), "depth" : 25 * mm});
        }
    });
